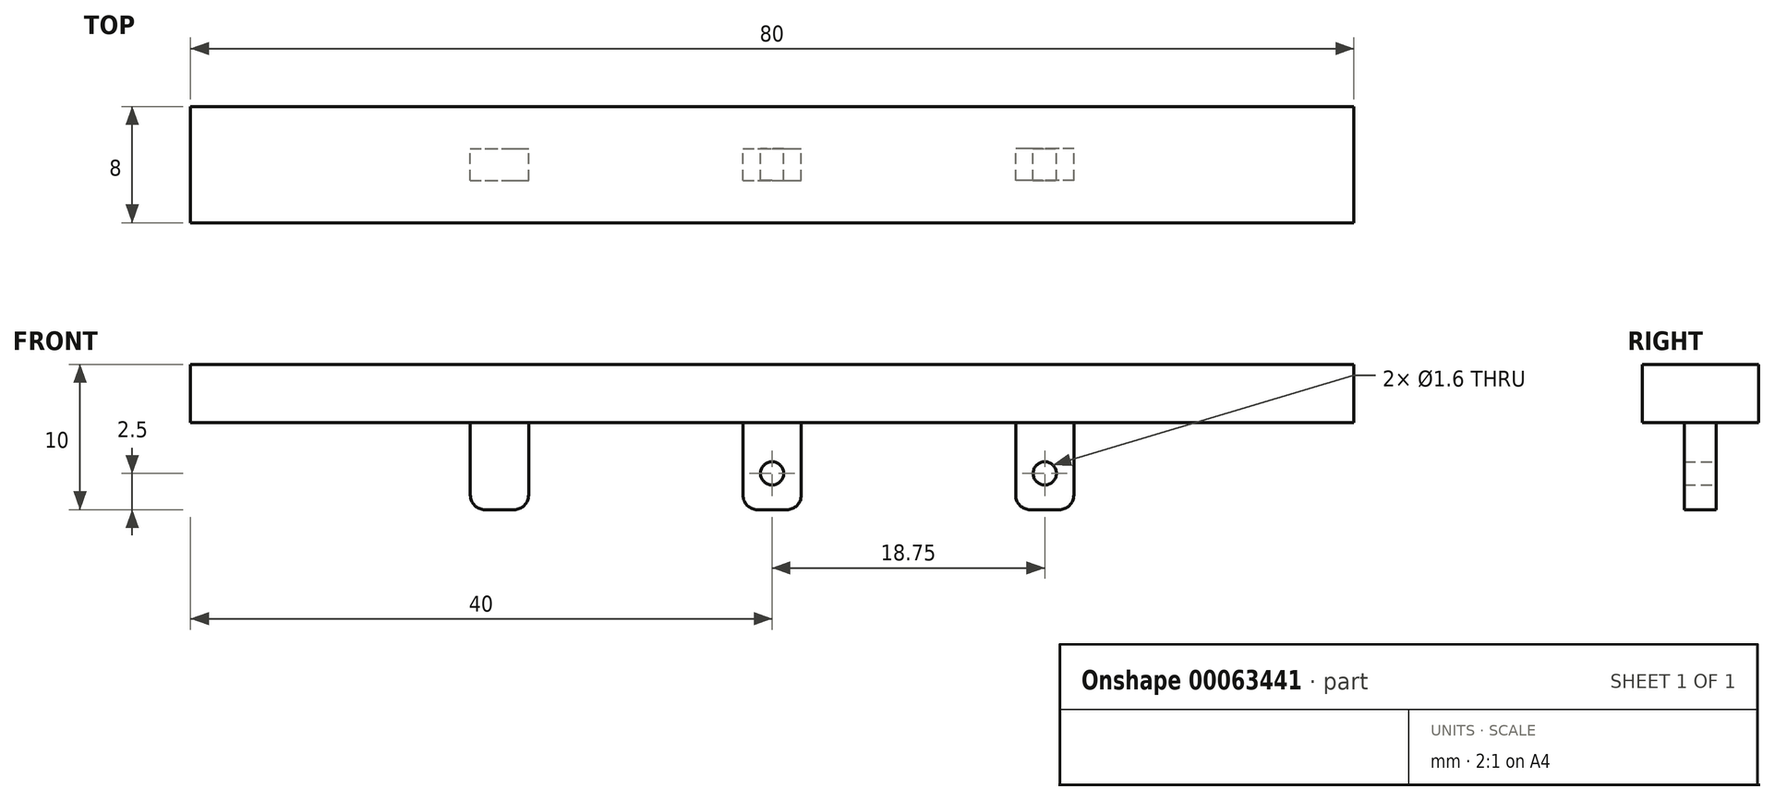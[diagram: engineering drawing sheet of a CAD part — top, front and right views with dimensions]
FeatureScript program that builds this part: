
annotation { "Feature Type Name" : "Feature", "Feature Type Description" : "" }
export const myFeature = defineFeature(function(context is Context, id is Id, definition is map)
    precondition{}
    {
        {
            var Q0;
            Q0=qCreatedBy(makeId("Front.planeOp"),FACE);
            var sketch = newSketch(context, id + "F0", { "sketchPlane" : qUnion([Q0])});
            skLineSegment(sketch, "E0", {"start": v(-40, 0) * mm, "end": v(-40, 4) * mm});
            skLineSegment(sketch, "E1", {"start": v(-40, 4) * mm, "end": v(0, 4) * mm});
            skLineSegment(sketch, "E2", {"start": v(-40, 0) * mm, "end": v(0, 0) * mm});
            skLineSegment(sketch, "E3.MirrorCS", {"start": v(40, 0) * mm, "end": v(40, 4) * mm});
            skLineSegment(sketch, "E4.MirrorCS", {"start": v(40, 0) * mm, "end": v(0, 0) * mm});
            skLineSegment(sketch, "E5.MirrorCS", {"start": v(40, 4) * mm, "end": v(0, 4) * mm});
            skSolve(sketch);
        }
        {
            var Q0;
            Q0 = qSketchRegion(id + "F0", true);
            extrude(context, id + "F1", {"entities" : qUnion([Q0]), "depth" : 8 * mm});
        }
        {
            var Q0;
            Q0=makeQuery(id+"F1.opExtrude","SWEPT_FACE",FACE,{"disambiguationData":[OSD([sQuery(id+"F0.wireOp",EDGE,"E2"),sQuery(id+"F0.wireOp",EDGE,"E4.MirrorCS")])]});
            var sketch = newSketch(context, id + "F2", { "sketchPlane" : qUnion([Q0])});
            skLineSegment(sketch, "E6", {"start": v(-40, 4) * mm, "end": v(40, 4) * mm, "construction": true});
            skLineSegment(sketch, "E7.bottom", {"start": v(-20.75, 5.1) * mm, "end": v(-16.75, 5.1) * mm});
            skLineSegment(sketch, "E7.top", {"start": v(-20.75, 2.9) * mm, "end": v(-16.75, 2.9) * mm});
            skLineSegment(sketch, "E7.left", {"start": v(-20.75, 5.1) * mm, "end": v(-20.75, 2.9) * mm});
            skLineSegment(sketch, "E7.right", {"start": v(-16.75, 5.1) * mm, "end": v(-16.75, 2.9) * mm});
            skPoint(sketch, "E8", {"position": v(-20.75, 4) * mm});
            skPoint(sketch, "E9", {"position": v(-18.75, 2.9) * mm});
            skLineSegment(sketch, "E10.MirrorCS", {"start": v(20.75, 5.1) * mm, "end": v(20.75, 2.9) * mm});
            skPoint(sketch, "E11.MirrorP", {"position": v(20.75, 4) * mm});
            skLineSegment(sketch, "E12.MirrorCS", {"start": v(16.75, 5.1) * mm, "end": v(16.75, 2.9) * mm});
            skLineSegment(sketch, "E13.MirrorCS", {"start": v(20.75, 2.9) * mm, "end": v(16.75, 2.9) * mm});
            skLineSegment(sketch, "E14.MirrorCS", {"start": v(20.75, 5.1) * mm, "end": v(16.75, 5.1) * mm});
            skPoint(sketch, "E15.MirrorP", {"position": v(18.75, 2.9) * mm});
            skLineSegment(sketch, "E16.bottom", {"start": v(-2, 5.1) * mm, "end": v(2, 5.1) * mm});
            skLineSegment(sketch, "E16.top", {"start": v(-2, 2.9) * mm, "end": v(2, 2.9) * mm});
            skLineSegment(sketch, "E16.left", {"start": v(-2, 5.1) * mm, "end": v(-2, 2.9) * mm});
            skLineSegment(sketch, "E16.right", {"start": v(2, 5.1) * mm, "end": v(2, 2.9) * mm});
            skPoint(sketch, "E17", {"position": v(0, 2.9) * mm});
            skSolve(sketch);
        }
        {
            var Q0;
            Q0=makeQuery(id+"F2.imprint","IMPRINT",FACE,{"disambiguationData":[TD([[makeQuery(id+"F2.imprint","IMPRINT",EDGE,{"derivedFrom":sQuery(id+"F2.wireOp",EDGE,"E7.bottom")}),-1.0]])]});
            var Q1;
            Q1=makeQuery(id+"F2.imprint","IMPRINT",FACE,{"disambiguationData":[TD([[makeQuery(id+"F2.imprint","IMPRINT",EDGE,{"derivedFrom":sQuery(id+"F2.wireOp",EDGE,"E10.MirrorCS")}),-1.0]])]});
            var Q2;
            Q2=makeQuery(id+"F2.imprint","IMPRINT",FACE,{"disambiguationData":[TD([[makeQuery(id+"F2.imprint","IMPRINT",EDGE,{"derivedFrom":sQuery(id+"F2.wireOp",EDGE,"E16.bottom")}),-1.0]])]});
            extrude(context, id + "F3", {"entities" : qUnion([Q0, Q1, Q2]), "operationType" : NewBodyOperationType.ADD, "depth" : 6 * mm});
        }
        {
            var Q0;
            Q0=makeQuery(id+"F3.opExtrude","SWEPT_FACE",FACE,{"disambiguationData":[OSD([sQuery(id+"F2.wireOp",EDGE,"E13.MirrorCS")])]});
            var sketch = newSketch(context, id + "F4", { "sketchPlane" : qUnion([Q0])});
            skCircle(sketch, "E18", {"center": v(-18.75, -3.5) * mm, "radius": 0.8 * mm});
            skPoint(sketch, "E18.centerSnap0", {"position": v(-18.75, -6) * mm});
            skCircle(sketch, "E19.MirrorC", {"center": v(18.75, -3.5) * mm, "radius": 0.8 * mm});
            skCircle(sketch, "E20", {"center": v(0, -3.5) * mm, "radius": 0.8 * mm});
            skSolve(sketch);
        }
        {
            var Q0;
            Q0=makeQuery(id+"F4.imprint","IMPRINT",FACE,{"disambiguationData":[TD([[makeQuery(id+"F4.imprint","IMPRINT",EDGE,{"derivedFrom":sQuery(id+"F4.wireOp",EDGE,"E18")}),1.0]])]});
            var Q1;
            Q1=makeQuery(id+"F4.imprint","IMPRINT",FACE,{"disambiguationData":[TD([[makeQuery(id+"F4.imprint","IMPRINT",EDGE,{"derivedFrom":sQuery(id+"F4.wireOp",EDGE,"E19.MirrorC")}),-1.0]])]});
            var Q2;
            Q2=makeQuery(id+"F4.imprint","IMPRINT",FACE,{"disambiguationData":[TD([[makeQuery(id+"F4.imprint","IMPRINT",EDGE,{"derivedFrom":sQuery(id+"F4.wireOp",EDGE,"E20")}),1.0]])]});
            extrude(context, id + "F5", {"entities" : qUnion([Q0, Q1, Q2]), "operationType" : NewBodyOperationType.REMOVE, "endBound" : BoundingType.THROUGH_ALL, "oppositeDirection" : true, "depth" : 25 * mm});
        }
        {
            var Q0;
            Q0=makeQuery(id+"F3.opExtrude","CAP_EDGE",EDGE,{"disambiguationData":[OSD([sQuery(id+"F2.wireOp",EDGE,"E10.MirrorCS")])],"isStart":false});
            var Q1;
            Q1=makeQuery(id+"F3.opExtrude","CAP_EDGE",EDGE,{"disambiguationData":[OSD([sQuery(id+"F2.wireOp",EDGE,"E12.MirrorCS")])],"isStart":false});
            var Q2;
            Q2=makeQuery(id+"F3.opExtrude","CAP_EDGE",EDGE,{"disambiguationData":[OSD([sQuery(id+"F2.wireOp",EDGE,"E7.right")])],"isStart":false});
            var Q3;
            Q3=makeQuery(id+"F3.opExtrude","CAP_EDGE",EDGE,{"disambiguationData":[OSD([sQuery(id+"F2.wireOp",EDGE,"E7.left")])],"isStart":false});
            var Q4;
            Q4=makeQuery(id+"F3.opExtrude","CAP_EDGE",EDGE,{"disambiguationData":[OSD([sQuery(id+"F2.wireOp",EDGE,"E16.left")])],"isStart":false});
            var Q5;
            Q5=makeQuery(id+"F3.opExtrude","CAP_EDGE",EDGE,{"disambiguationData":[OSD([sQuery(id+"F2.wireOp",EDGE,"E16.right")])],"isStart":false});
            fillet(context, id + "F6", {"entities" : qUnion([Q0, Q1, Q2, Q3, Q4, Q5]), "radius" : 1 * mm, "tangentPropagation" : true, "allowEdgeOverflow" : false});
        }
    });
